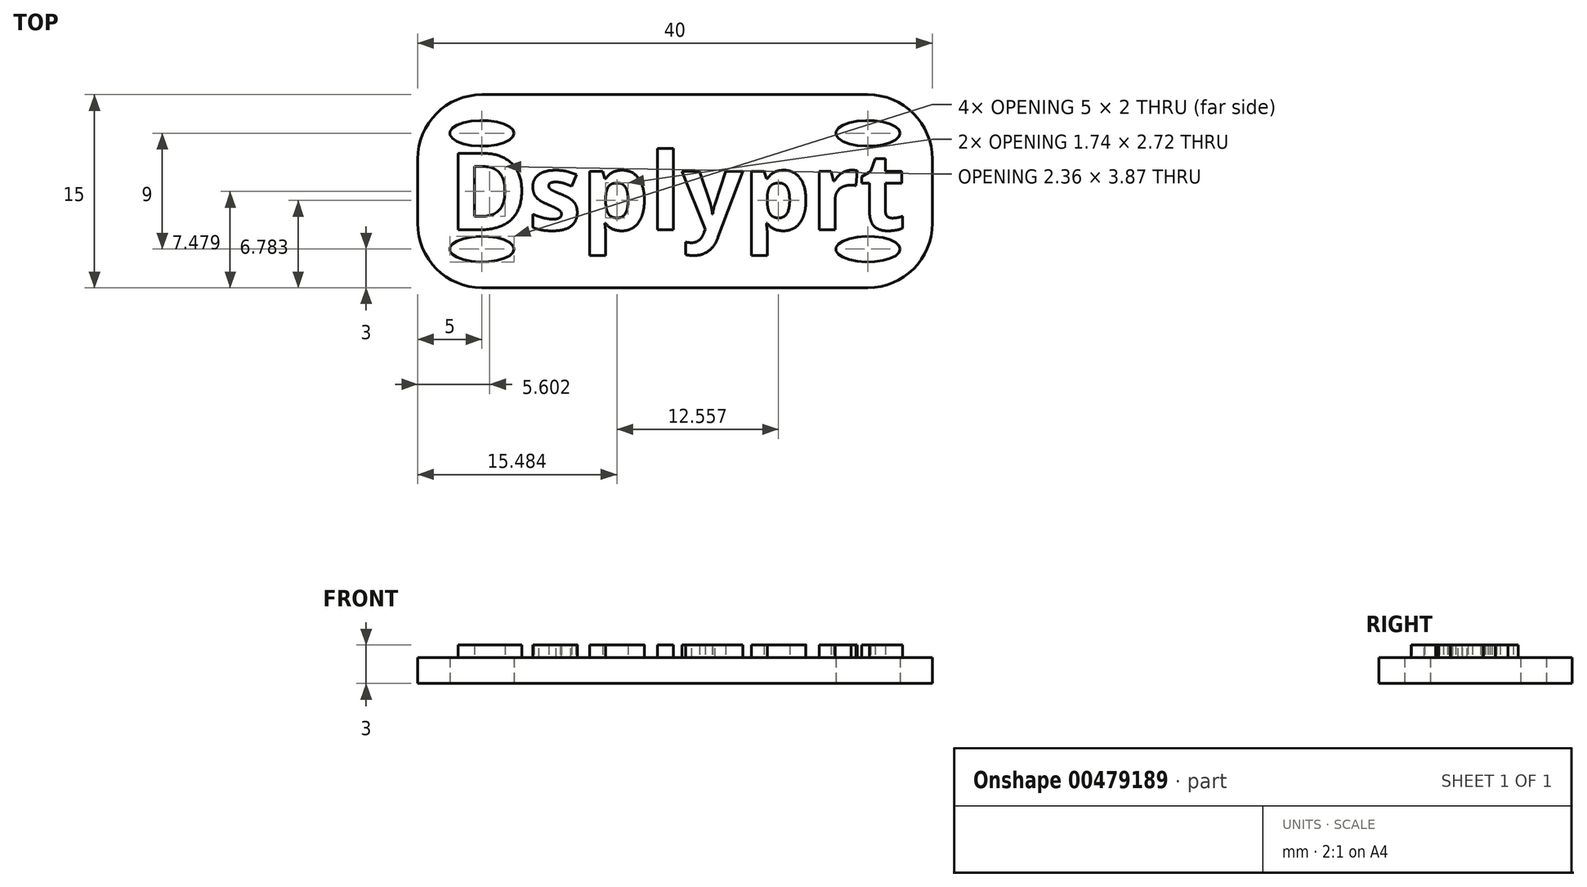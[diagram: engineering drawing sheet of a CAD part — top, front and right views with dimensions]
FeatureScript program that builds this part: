
annotation { "Feature Type Name" : "Feature", "Feature Type Description" : "" }
export const myFeature = defineFeature(function(context is Context, id is Id, definition is map)
    precondition{}
    {
        {
            var Q0;
            Q0=qCreatedBy(makeId("Top.planeOp"),FACE);
            var sketch = newSketch(context, id + "F0", { "sketchPlane" : qUnion([Q0])});
            skLineSegment(sketch, "E0.bottom", {"start": v(20, -7.5) * mm, "end": v(-20, -7.5) * mm});
            skLineSegment(sketch, "E0.top", {"start": v(20, 7.5) * mm, "end": v(-20, 7.5) * mm});
            skLineSegment(sketch, "E0.left", {"start": v(20, -7.5) * mm, "end": v(20, 7.5) * mm});
            skLineSegment(sketch, "E0.right", {"start": v(-20, -7.5) * mm, "end": v(-20, 7.5) * mm});
            skPoint(sketch, "E0.middle", {"position": v(0, 0) * mm});
            skLineSegment(sketch, "E1", {"start": v(-20, -4.5) * mm, "end": v(20, -4.5) * mm, "construction": true});
            skPoint(sketch, "E2", {"position": v(-15, -4.5) * mm});
            skEllipse(sketch, "E3", {"center": v(-15, -4.5) * mm, "majorRadius": 2.5 * mm, "minorRadius": 1 * mm, "majorAxis": v(1, 0)});
            skEllipse(sketch, "E4.1.0.0", {"center": v(15, -4.5) * mm, "majorRadius": 2.5 * mm, "minorRadius": 1 * mm, "majorAxis": v(1, 0)});
            skLineSegment(sketch, "E4.direction1", {"start": v(-15, -4.5) * mm, "end": v(15, -4.5) * mm, "construction": true});
            skLineSegment(sketch, "E5", {"start": v(20, 0) * mm, "end": v(-20, 0) * mm, "construction": true});
            skEllipse(sketch, "E6.MirrorC", {"center": v(15, 4.5) * mm, "majorRadius": 2.5 * mm, "minorRadius": 1 * mm, "majorAxis": v(1, 0)});
            skEllipse(sketch, "E7.MirrorC", {"center": v(-15, 4.5) * mm, "majorRadius": 2.5 * mm, "minorRadius": 1 * mm, "majorAxis": v(1, 0)});
            skSolve(sketch);
        }
        {
            var Q0;
            Q0=makeQuery(id+"F0.imprint","IMPRINT",FACE,{"disambiguationData":[TD([[makeQuery(id+"F0.imprint","IMPRINT",EDGE,{"derivedFrom":sQuery(id+"F0.wireOp",EDGE,"E0.bottom")}),-1.0]])]});
            extrude(context, id + "F1", {"entities" : qUnion([Q0]), "depth" : 2 * mm});
        }
        {
            var Q0;
            Q0=makeQuery(id+"F1.opExtrude","CAP_FACE",FACE,{"disambiguationData":[OSD([sQuery(id+"F0.wireOp",EDGE,"E0.bottom"),sQuery(id+"F0.wireOp",EDGE,"E0.top"),sQuery(id+"F0.wireOp",EDGE,"E0.left"),sQuery(id+"F0.wireOp",EDGE,"E0.right"),sQuery(id+"F0.wireOp",EDGE,"E3"),sQuery(id+"F0.wireOp",EDGE,"E4.1.0.0"),sQuery(id+"F0.wireOp",EDGE,"E6.MirrorC"),sQuery(id+"F0.wireOp",EDGE,"E7.MirrorC")])],"isStart":false});
            var sketch = newSketch(context, id + "F2", { "sketchPlane" : qUnion([Q0])});
            skText(sketch, "E8", { "text": "Dsplyprt\n", "fontName": "OpenSans-Bold.ttf"});
            const initialGuessF2  = {"E8": [-0.01759, -0.003, 1, 0, 0.006]};
            skSetInitialGuess(sketch, initialGuessF2);
            skSolve(sketch);
        }
        {
            var Q0;
            Q0=qSketchRegion(id+"F2",true);
            extrude(context, id + "F3", {"entities" : qUnion([Q0]), "depth" : 1 * mm});
        }
        {
            var Q0;
            Q0=makeQuery(id+"F1.opExtrude","SWEPT_EDGE",EDGE,{"disambiguationData":[OSD([sQuery(id+"F0.wireOp",EDGE,"E0.bottom"),sQuery(id+"F0.wireOp",EDGE,"E0.right")])]});
            var Q1;
            Q1=makeQuery(id+"F1.opExtrude","SWEPT_EDGE",EDGE,{"disambiguationData":[OSD([sQuery(id+"F0.wireOp",EDGE,"E0.bottom"),sQuery(id+"F0.wireOp",EDGE,"E0.left")])]});
            var Q2;
            Q2=makeQuery(id+"F1.opExtrude","SWEPT_EDGE",EDGE,{"disambiguationData":[OSD([sQuery(id+"F0.wireOp",EDGE,"E0.top"),sQuery(id+"F0.wireOp",EDGE,"E0.left")])]});
            var Q3;
            Q3=makeQuery(id+"F1.opExtrude","SWEPT_EDGE",EDGE,{"disambiguationData":[OSD([sQuery(id+"F0.wireOp",EDGE,"E0.top"),sQuery(id+"F0.wireOp",EDGE,"E0.right")])]});
            fillet(context, id + "F4", {"entities" : qUnion([Q0, Q1, Q2, Q3]), "radius" : 5 * mm, "tangentPropagation" : true, "allowEdgeOverflow" : false});
        }
    });
